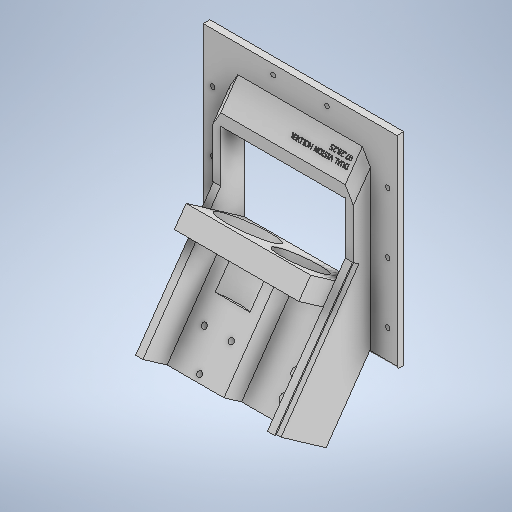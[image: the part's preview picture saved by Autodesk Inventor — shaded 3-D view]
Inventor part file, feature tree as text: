
AUTODESK INVENTOR PART (.ipt)
format: ipt  version: 2025.2 (Build 292293000, 293)  size: 1,339,904 bytes
history: native  units: in
note: dims shown in document units (in); Inventor stores cm internally (conversion verified against a paired STEP export)
features: sketch x42, extrude x37, plane x5, projected_geometry x3, move_body x1, chamfer x1, fillet x1, hole x1
ambient origin geometry x8: Origin, YZ Plane, XZ Plane, XY Plane, X Axis, Y Axis, Z Axis, Center Point
bodies: Solid1 (feature_tree)
feature tree (91):
  extrude  "Extrusion1"  Depth=0.1969in TaperAngle=0.0deg
  move_body  "Move Body1"
  plane  "Work Plane1"
  sketch  "Sketch5"  dims[d5=1.7717in d6=1.7717in d7=1.7717in d8=1.7717in d9=0.8108in d10=90.0deg d11=0.0787in d12=0.3701in d13=0.4252in d14=0.1362in d15=-0.0984in d16=-0.0591in d17=0.0in]
  plane  "Work Plane2"
  extrude  "Extrusion4"  TaperAngle=0.0deg  [1 undecoded]
  extrude  "Extrusion6"  Depth=0.2405in
  extrude  "Extrusion8"  Depth=2.5591in TaperAngle=0.0deg
  chamfer  "Chamfer1"  [1 undecoded]
  extrude  "Extrusion11"  Depth=0.2362in
  plane  "Work Plane3"
  extrude  "Extrusion13"  Depth=0.1969in TaperAngle=0.0deg
  plane  "Work Plane4"
  plane  "Work Plane6"
  extrude  "Extrusion21"  Depth=0.5027in
  extrude  "Extrusion22"  Depth=0.5027in
  extrude  "Extrusion25"  Depth=1.1811in TaperAngle=0.0deg
  extrude  "Extrusion26"  Depth=0.1969in
  sketch  "Sketch33"  dims[d100=3.6403in d101=2.7717in]
  extrude  "Extrusion27"  Depth=0.2362in TaperAngle=0.0deg
  extrude  "Extrusion29"  Depth=3.6403in
  extrude  "Extrusion28"  Depth=0.6299in TaperAngle=0.0deg
  sketch  "Sketch36"  dims[d124=0.9712in d125=0.0in d126=0.5906in d127=0.0in d128=11.3469in d129=0.0in]
  extrude  "Extrusion30"  Depth=0.7874in
  extrude  "Extrusion31"  Depth=0.5906in TaperAngle=0.0deg
  sketch  "Sketch39"  dims[d149=0.2756in d150=0.0in d151=0.0in]
  fillet  "Fillet1"  Radius=11.3469in
  extrude  "Extrusion33"  Depth=0.6299in
  extrude  "Extrusion34"  Depth=0.2756in
  extrude  "Extrusion35"  TaperAngle=0.0deg  [1 undecoded]
  sketch  "Sketch45"  dims[d170=4.7244in d171=0.0in d174=0.0in d175=0.0in]
  extrude  "Extrusion37"  Depth=0.1181in TaperAngle=0.0deg
  extrude  "Extrusion38"  Depth=0.1181in TaperAngle=0.0deg
  extrude  "Extrusion40"  Depth=0.1181in TaperAngle=0.0deg
  extrude  "Extrusion41"  TaperAngle=0.0deg  [1 undecoded]
  extrude  "Extrusion43"  TaperAngle=0.0deg  [1 undecoded]
  extrude  "Extrusion44"  TaperAngle=0.0deg  [1 undecoded]
  extrude  "Extrusion46"  Depth=0.4724in
  extrude  "Extrusion47"  Depth=0.0394in TaperAngle=0.0deg
  extrude  "Extrusion48"  Depth=3.9671in TaperAngle=0.0deg
  sketch  "Sketch61"  dims[d253=60.0deg d254=0.3937in]
  extrude  "Extrusion50"  Depth=0.1969in
  extrude  "Extrusion51"  TaperAngle=60.0deg  [1 undecoded]
  extrude  "Extrusion52"  Depth=0.1969in
  extrude  "Extrusion53"  Depth=0.3937in
  extrude  "Extrusion54"  Depth=0.3937in
  extrude  "Extrusion57"  Depth=0.1181in TaperAngle=0.0deg
  extrude  "Extrusion59"  Depth=0.3937in TaperAngle=0.0deg
  extrude  "Extrusion60"  TaperAngle=0.0deg  [1 undecoded]
  extrude  "Extrusion61"  Depth=1.0236in
  extrude  "Extrusion62"  TaperAngle=0.0deg  [1 undecoded]
  sketch  "Sketch1"  dims[d1=0.5512in d2=0.1969in d3=0.0in]
  sketch  "Sketch6"  dims[d18=0.2749in d24=0.2405in]
  sketch  "Sketch8"  dims[d25=2.7559in d26=0.0in d29=2.5591in d30=0.0in d36=0.0in d37=0.0in]
  sketch  "Sketch12"  dims[d42=0.2362in d43=0.2362in]
  sketch  "Sketch15"  dims[d52=0.2362in d53=0.0787in d54=45.0deg d55=0.1969in d56=0.0in]
  sketch  "Sketch17"  dims[d59=0.5906in d60=0.0in d76=0.5027in]
  sketch  "Sketch27"  dims[d77=0.5027in d78=0.5027in]
  sketch  "Sketch28"  dims[d79=0.5027in d81=1.1811in d82=0.0in]
  sketch  "Sketch31"  dims[d83=0.0in d84=0.0in d91=0.1969in]
  sketch  "Sketch32"  dims[d94=0.2362in d95=0.0in d96=0.2362in d97=0.0in]
  sketch  "Sketch34"  dims[d112=1.9685in d113=0.6299in d114=0.0in]
  sketch  "Sketch35"  dims[d115=0.1575in d117=0.1575in d122=0.7874in d123=0.9331in]
  sketch  "Sketch37"  dims[d130=11.3469in d131=0.0in d141=0.6299in]
  sketch  "Sketch38"  dims[d142=0.0787in d147=0.2756in]
  sketch  "Sketch41"  dims[d154=0.1181in d155=0.0in d156=0.1181in d157=0.0in]
  sketch  "Sketch42"  dims[d158=0.4724in d160=0.1181in d161=0.0in]
  sketch  "Sketch44"  dims[d164=0.1181in d165=0.0in d168=0.5906in d169=0.0in]
  projected_geometry  "Projected Loop2"
  projected_geometry  "Projected Loop3"
  projected_geometry  "Projected Loop5"
  sketch  "Sketch47"  dims[d176=0.7313in d177=0.0in d186=0.0in d187=0.0in]
  sketch  "Sketch49"  dims[d188=0.0in d189=0.0in d194=0.0in d195=0.0in]
  sketch  "Sketch50"  dims[d196=0.5906in d197=0.4724in]
  sketch  "Sketch52"  dims[d198=0.0591in d199=0.0in d200=0.0394in d201=0.0in]
  sketch  "Sketch53"  dims[d235=6.1063in d236=0.0in d244=3.9671in d245=0.0in]
  sketch  "Sketch56"  dims[d246=0.9963in d248=0.1969in]
  sketch  "Sketch58"  dims[d249=0.1378in d250=60.0deg]
  sketch  "Sketch59"  dims[d251=0.1969in d252=0.1378in]
  sketch  "Sketch63"  dims[d255=0.3937in d256=0.3937in]
  sketch  "Sketch64"  dims[d257=0.1181in d258=0.0in d259=0.0787in d260=0.0in]
  sketch  "Sketch65"  dims[d261=1.9685in d262=0.0in d271=0.3937in d272=0.0in]
  sketch  "Sketch66"  dims[d275=0.3937in d276=0.0in d277=0.0in d278=0.0in]
  sketch  "Sketch67"  dims[d279=1.3386in d280=1.0236in]
  sketch  "Sketch70"  dims[d281=1.4764in d282=0.0in d283=0.0in]
  sketch  "Sketch72"  dims[d284=1.5748in d287=1.1614in]
  sketch  "Sketch75"  dims[d288=0.8512in]
  sketch  "Sketch76"  dims[d289=0.6299in d290=0.0in]
  sketch  "Sketch77"  dims[d38=0.0197in d39=0.0344in d57=0.0197in d58=0.0344in d159=0.0344in d178=0.0in d179=0.0in d180=0.0in d181=0.0in d202=0.0197in d203=0.0344in]
  sketch  "Sketch2"  dims[d4=0.315in]
  hole  "Hole1"  [1 undecoded]
note: 10 required parameter values undecoded (feature->parameter linkage not recoverable at this tier; creation-order binding heuristic only, values carry confidence <= 0.55)
